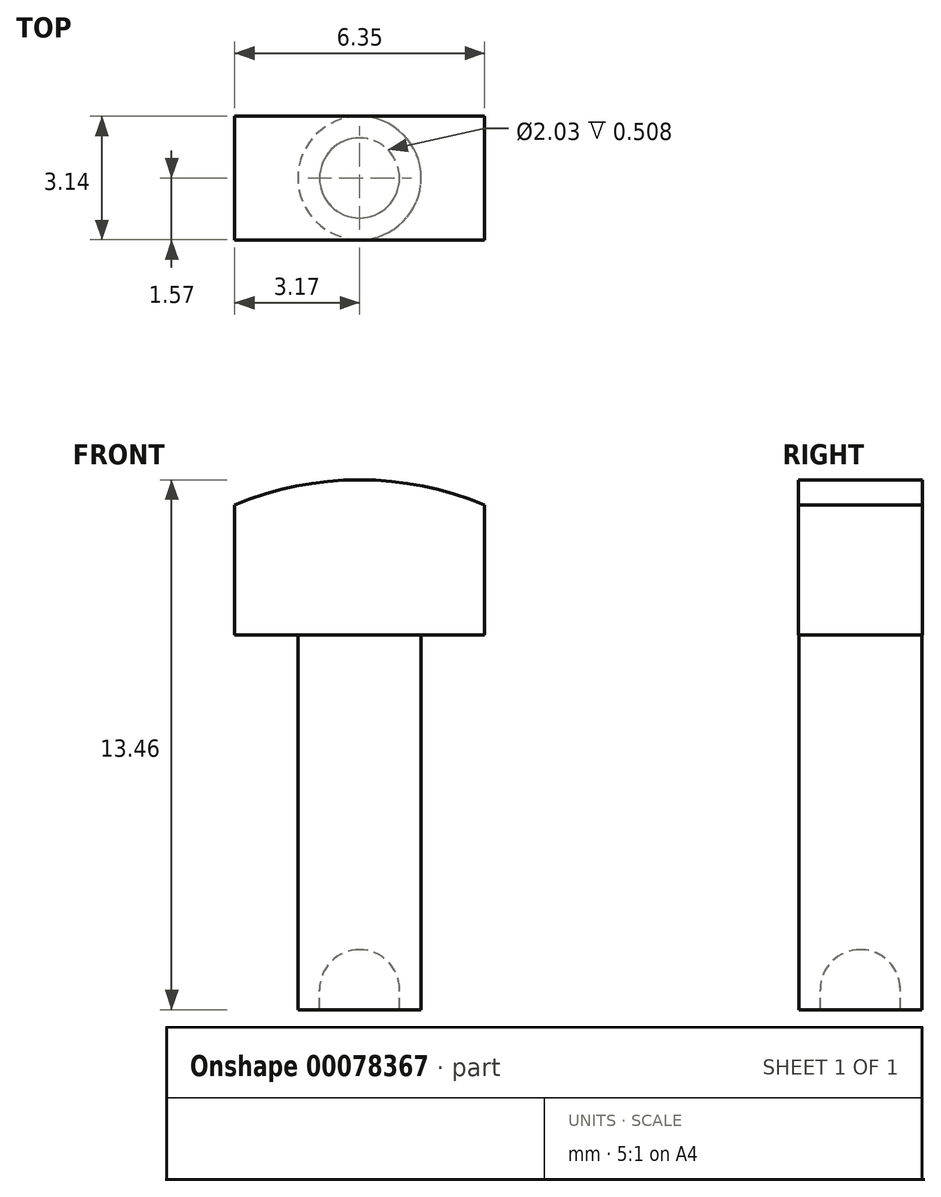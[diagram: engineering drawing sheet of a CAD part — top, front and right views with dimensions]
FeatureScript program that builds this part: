
annotation { "Feature Type Name" : "Feature", "Feature Type Description" : "" }
export const myFeature = defineFeature(function(context is Context, id is Id, definition is map)
    precondition{}
    {
        {
            var Q0;
            Q0=qCreatedBy(makeId("Top.planeOp"),FACE);
            var sketch = newSketch(context, id + "F0", { "sketchPlane" : qUnion([Q0])});
            skCircle(sketch, "E0", {"center": v(0, 0) * mm, "radius": 1.57 * mm});
            skSolve(sketch);
        }
        {
            var Q0;
            Q0 = qSketchRegion(id + "F0", true);
            extrude(context, id + "F1", {"entities" : qUnion([Q0]), "depth" : 9.52 * mm});
        }
        {
            var Q0;
            Q0=qCreatedBy(makeId("Front.planeOp"),FACE);
            var sketch = newSketch(context, id + "F2", { "sketchPlane" : qUnion([Q0])});
            skArc(sketch, "E1", {"start": v(3.17, 12.83) * mm, "mid": v(0, 13.46) * mm, "end": v(-3.18, 12.83) * mm});
            skLineSegment(sketch, "E2", {"start": v(0, 0) * mm, "end": v(0, 5.2) * mm});
            skLineSegment(sketch, "E3", {"start": v(0, 9.53) * mm, "end": v(-3.18, 9.53) * mm});
            skLineSegment(sketch, "E4", {"start": v(-3.18, 9.53) * mm, "end": v(-3.18, 12.83) * mm});
            skLineSegment(sketch, "E5.MirrorCS", {"start": v(0, 9.53) * mm, "end": v(3.18, 9.53) * mm});
            skLineSegment(sketch, "E6.MirrorCS", {"start": v(3.18, 9.53) * mm, "end": v(3.18, 12.83) * mm});
            skSolve(sketch);
        }
        {
            var Q0;
            Q0 = qSketchRegion(id + "F2", true);
            extrude(context, id + "F3", {"entities" : qUnion([Q0]), "operationType" : NewBodyOperationType.ADD, "endBound" : BoundingType.SYMMETRIC, "depth" : 3.14 * mm});
        }
        {
            var Q0;
            Q0=qCreatedBy(makeId("Right.planeOp"),FACE);
            var sketch = newSketch(context, id + "F4", { "sketchPlane" : qUnion([Q0])});
            skArc(sketch, "E7", {"start": v(0, 1.52) * mm, "mid": v(-0.72, 1.23) * mm, "end": v(-1.02, 0.5) * mm});
            skLineSegment(sketch, "E8", {"start": v(-1.02, 0.5) * mm, "end": v(-1.02, 0) * mm});
            skLineSegment(sketch, "E9", {"start": v(0, 0) * mm, "end": v(-1.02, 0) * mm});
            skLineSegment(sketch, "E10", {"start": v(0, 0) * mm, "end": v(0, 1.52) * mm});
            skSolve(sketch);
        }
        {
            var Q0;
            Q0 = qSketchRegion(id + "F4", true);
            var Q1;
            Q1=sQuery(id+"F4.wireOp",EDGE,"E10");
            revolve(context, id + "F5", {"operationType" : NewBodyOperationType.REMOVE, "entities" : qUnion([Q0]), "axis" : qUnion([Q1]), "revolveType" : RevolveType.FULL, "oppositeDirection" : true});
        }
    });
